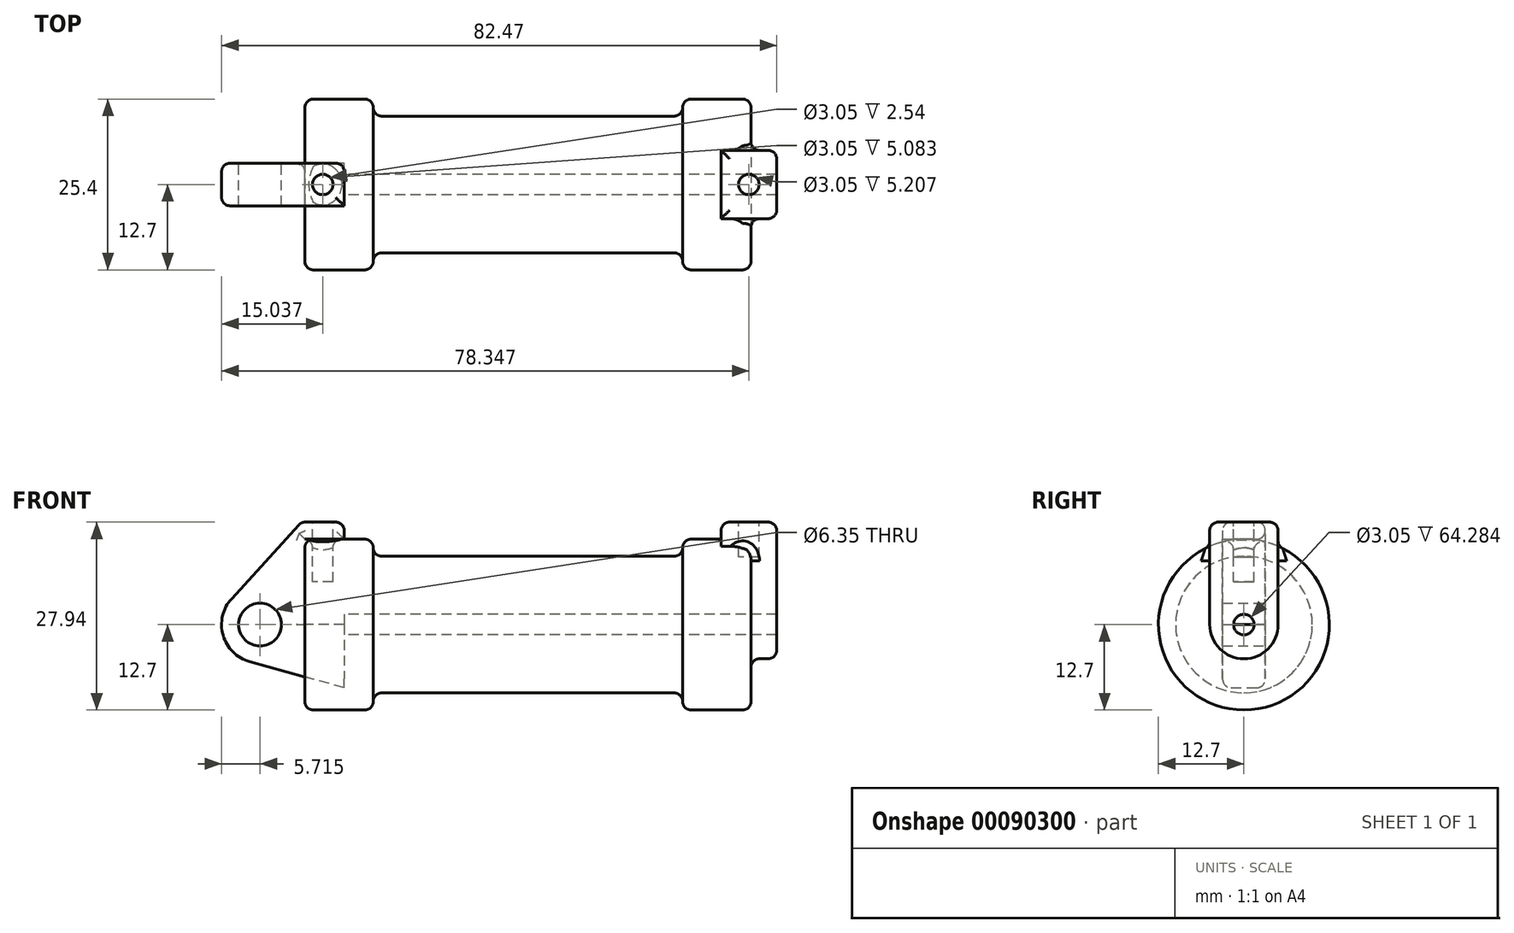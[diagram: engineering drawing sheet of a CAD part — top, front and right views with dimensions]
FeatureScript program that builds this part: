
annotation { "Feature Type Name" : "Feature", "Feature Type Description" : "" }
export const myFeature = defineFeature(function(context is Context, id is Id, definition is map)
    precondition{}
    {
        {
            var Q0;
            Q0=qCreatedBy(makeId("Front.planeOp"),FACE);
            var sketch = newSketch(context, id + "F0", { "sketchPlane" : qUnion([Q0])});
            skLineSegment(sketch, "E0", {"start": v(0, 0) * mm, "end": v(0, 12.7) * mm});
            skLineSegment(sketch, "E1", {"start": v(0, 12.7) * mm, "end": v(10.16, 12.7) * mm});
            skLineSegment(sketch, "E2", {"start": v(10.16, 12.7) * mm, "end": v(10.16, 10.16) * mm});
            skLineSegment(sketch, "E3", {"start": v(10.16, 10.16) * mm, "end": v(56.13, 10.16) * mm});
            skLineSegment(sketch, "E4", {"start": v(56.13, 10.16) * mm, "end": v(56.13, 12.7) * mm});
            skLineSegment(sketch, "E5", {"start": v(56.13, 12.7) * mm, "end": v(66.3, 12.7) * mm});
            skLineSegment(sketch, "E6", {"start": v(66.3, 12.7) * mm, "end": v(66.3, 0) * mm});
            skLineSegment(sketch, "E7", {"start": v(66.3, 0) * mm, "end": v(0, 0) * mm});
            skLineSegment(sketch, "E8", {"start": v(5.84, 15.24) * mm, "end": v(-0.5, 15.24) * mm});
            skLineSegment(sketch, "E9", {"start": v(-0.5, 15.24) * mm, "end": v(-10.88, 3.85) * mm});
            skLineSegment(sketch, "E10", {"start": v(0, 0) * mm, "end": v(-6.65, 0) * mm});
            skCircle(sketch, "E11", {"center": v(-6.65, 0) * mm, "radius": 5.72 * mm});
            skCircle(sketch, "E12", {"center": v(-6.65, 0) * mm, "radius": 3.18 * mm});
            skLineSegment(sketch, "E13", {"start": v(5.84, 15.24) * mm, "end": v(5.84, -9.4) * mm});
            skLineSegment(sketch, "E14", {"start": v(5.84, -9.4) * mm, "end": v(-8.18, -5.5) * mm});
            skSolve(sketch);
        }
        {
            var Q0;
            {var subQ0=sQuery(id+"F0.wireOp",EDGE,"E2");Q0=makeQuery(id+"F0.imprint","IMPRINT",FACE,{"disambiguationData":[TD([[makeQuery(id+"F0.imprint","IMPRINT",EDGE,{"derivedFrom":subQ0}),-1.0]])]});}
            var Q1;
            {var subQ0=sQuery(id+"F0.wireOp",EDGE,"E0");Q1=makeQuery(id+"F0.imprint","IMPRINT",FACE,{"disambiguationData":[TD([[makeQuery(id+"F0.imprint","IMPRINT",EDGE,{"derivedFrom":subQ0}),-1.0]])]});}
            var Q2;
            Q2=sQuery(id+"F0.wireOp",EDGE,"E7");
            revolve(context, id + "F1", {"entities" : qUnion([Q0, Q1]), "axis" : qUnion([Q2]), "revolveType" : RevolveType.FULL});
        }
        {
            var Q0;
            {var subQ3=sQuery(id+"F0.wireOp",EDGE,"E0");Q0=makeQuery(id+"F0.imprint","IMPRINT",FACE,{"disambiguationData":[TD([[makeQuery(id+"F0.imprint","IMPRINT",EDGE,{"derivedFrom":subQ3}),1.0]])]});}
            var Q1;
            {var subQ0=sQuery(id+"F0.wireOp",EDGE,"E14");Q1=makeQuery(id+"F0.imprint","IMPRINT",FACE,{"disambiguationData":[TD([[makeQuery(id+"F0.imprint","IMPRINT",EDGE,{"derivedFrom":subQ0}),-1.0]])]});}
            var Q2;
            {var subQ4=sQuery(id+"F0.wireOp",EDGE,"E12");Q2=makeQuery(id+"F0.imprint","IMPRINT",FACE,{"disambiguationData":[TD([[makeQuery(id+"F0.imprint","IMPRINT",EDGE,{"derivedFrom":subQ4}),-1.0]])]});}
            extrude(context, id + "F2", {"entities" : qUnion([Q0, Q1, Q2]), "endBound" : BoundingType.SYMMETRIC, "depth" : 6.35 * mm});
        }
        {
            var Q0;
            Q0=makeQuery(id+"F1.opRevolve","SWEPT_FACE",FACE,{"disambiguationData":[OSD([sQuery(id+"F0.wireOp",EDGE,"E6")])]});
            var sketch = newSketch(context, id + "F3", { "sketchPlane" : qUnion([Q0])});
            skCircle(sketch, "E15", {"center": v(0, 0) * mm, "radius": 1.52 * mm});
            skCircle(sketch, "E16", {"center": v(0, 0) * mm, "radius": 5.08 * mm});
            skLineSegment(sketch, "E17", {"start": v(-5.08, 15.24) * mm, "end": v(-5.08, 0) * mm});
            skLineSegment(sketch, "E18", {"start": v(5.08, 15.24) * mm, "end": v(5.08, 0) * mm});
            skLineSegment(sketch, "E19", {"start": v(-5.08, 15.24) * mm, "end": v(5.08, 15.24) * mm});
            skSolve(sketch);
        }
        {
            var Q0;
            {var subQ0=sQuery(id+"F3.wireOp",EDGE,"E19");Q0=makeQuery(id+"F3.imprint","IMPRINT",FACE,{"disambiguationData":[TD([[makeQuery(id+"F3.imprint","IMPRINT",EDGE,{"derivedFrom":subQ0}),-1.0]])]});}
            var Q1;
            {var subQ0=sQuery(id+"F3.wireOp",EDGE,"E17");var subQ1=sQuery(id+"F3.wireOp",EDGE,"E16");var subQ2=makeQuery(id+"F3.imprint","INTERSECT",VERTEX,{"derivedFrom":[subQ1,subQ0]});Q1=makeQuery(id+"F3.imprint","IMPRINT",FACE,{"disambiguationData":[TD([[makeQuery(id+"F3.imprint","IMPRINT",EDGE,{"disambiguationData":[TD([[subQ2,1.0]])],"derivedFrom":subQ1}),-1.0]])]});}
            var Q2;
            Q2=makeQuery(id+"F3.imprint","IMPRINT",FACE,{"disambiguationData":[TD([[makeQuery(id+"F3.imprint","IMPRINT",EDGE,{"derivedFrom":sQuery(id+"F3.wireOp",EDGE,"E15")}),-1.0]])]});
            extrude(context, id + "F4", {"entities" : qUnion([Q0, Q1, Q2]), "operationType" : NewBodyOperationType.ADD, "endBound" : BoundingType.SYMMETRIC, "depth" : 7.62 * mm});
        }
        {
            var Q0;
            Q0=makeQuery(id+"F4.opExtrude","CAP_FACE",FACE,{"disambiguationData":[OSD([sQuery(id+"F3.wireOp",EDGE,"E15"),sQuery(id+"F3.wireOp",EDGE,"E16"),sQuery(id+"F3.wireOp",EDGE,"E17"),sQuery(id+"F3.wireOp",EDGE,"E18"),sQuery(id+"F3.wireOp",EDGE,"E19")])],"isStart":true});
            extrude(context, id + "F5", {"entities" : qUnion([Q0]), "operationType" : NewBodyOperationType.ADD, "endBound" : BoundingType.SYMMETRIC, "depth" : 1.27 * mm});
        }
        {
            var Q0;
            Q0=makeQuery(id+"F4.boolean.opBoolean","SPLIT",FACE,{"disambiguationData":[TD([makeQuery(id+"F4.opExtrude","SWEPT_FACE",FACE,{"disambiguationData":[OSD([sQuery(id+"F3.wireOp",EDGE,"E15")])]})])],"derivedFrom":makeQuery(id+"F1.opRevolve","SWEPT_FACE",FACE,{"disambiguationData":[OSD([sQuery(id+"F0.wireOp",EDGE,"E6")])]})});
            extrude(context, id + "F6", {"entities" : qUnion([Q0]), "operationType" : NewBodyOperationType.REMOVE, "endBound" : BoundingType.SYMMETRIC, "oppositeDirection" : true, "depth" : 120.95 * mm});
        }
        {
            var Q0;
            Q0=makeQuery(id+"F2.opExtrude","SWEPT_FACE",FACE,{"disambiguationData":[OSD([sQuery(id+"F0.wireOp",EDGE,"E8")])]});
            var sketch = newSketch(context, id + "F7", { "sketchPlane" : qUnion([Q0])});
            skCircle(sketch, "E20", {"center": v(2.67, 0) * mm, "radius": 1.52 * mm});
            skPoint(sketch, "E20.centerSnap0", {"position": v(2.67, 3.18) * mm});
            skPoint(sketch, "E20.centerSnap1", {"position": v(-0.5, 0) * mm});
            skSolve(sketch);
        }
        {
            var Q0;
            {var subQ0=sQuery(id+"F3.wireOp",EDGE,"E19");Q0=makeQuery(id+"F5.boolean.opBoolean","MERGE",FACE,{"derivedFrom":[makeQuery(id+"F4.opExtrude","SWEPT_FACE",FACE,{"disambiguationData":[OSD([subQ0])]}),makeQuery(id+"F5.opExtrude","SWEPT_FACE",FACE,{"disambiguationData":[OSD([subQ0])]})]});}
            var sketch = newSketch(context, id + "F8", { "sketchPlane" : qUnion([Q0])});
            skCircle(sketch, "E21", {"center": v(65.98, 0) * mm, "radius": 1.52 * mm});
            skPoint(sketch, "E21.centerSnap0", {"position": v(65.98, 5.08) * mm});
            skPoint(sketch, "E21.centerSnap1", {"position": v(61.85, 0) * mm});
            skSolve(sketch);
        }
        {
            var Q0;
            Q0=makeQuery(id+"F7.imprint","IMPRINT",FACE,{"disambiguationData":[TD([[makeQuery(id+"F7.imprint","IMPRINT",EDGE,{"derivedFrom":sQuery(id+"F7.wireOp",EDGE,"E20")}),1.0]])]});
            extrude(context, id + "F9", {"entities" : qUnion([Q0]), "operationType" : NewBodyOperationType.REMOVE, "endBound" : BoundingType.SYMMETRIC, "oppositeDirection" : true, "depth" : 17.78 * mm});
        }
        {
            var Q0;
            Q0=makeQuery(id+"F8.imprint","IMPRINT",FACE,{"disambiguationData":[TD([[makeQuery(id+"F8.imprint","IMPRINT",EDGE,{"derivedFrom":sQuery(id+"F8.wireOp",EDGE,"E21")}),1.0]])]});
            extrude(context, id + "F10", {"entities" : qUnion([Q0]), "operationType" : NewBodyOperationType.REMOVE, "endBound" : BoundingType.SYMMETRIC, "oppositeDirection" : true, "depth" : 10.4 * mm});
        }
        {
            var Q0;
            Q0=makeQuery(id+"F2.opExtrude","CAP_EDGE",EDGE,{"disambiguationData":[OSD([sQuery(id+"F0.wireOp",EDGE,"E8")])],"isStart":false});
            var Q1;
            Q1=makeQuery(id+"F2.opExtrude","SWEPT_EDGE",EDGE,{"disambiguationData":[OSD([sQuery(id+"F0.wireOp",EDGE,"E8"),sQuery(id+"F0.wireOp",EDGE,"E13")])]});
            var Q2;
            Q2=makeQuery(id+"F2.opExtrude","CAP_EDGE",EDGE,{"disambiguationData":[OSD([sQuery(id+"F0.wireOp",EDGE,"E8")])],"isStart":true});
            var Q3;
            Q3=makeQuery(id+"F2.opExtrude","CAP_EDGE",EDGE,{"disambiguationData":[OSD([sQuery(id+"F0.wireOp",EDGE,"E9")])],"isStart":false});
            var Q4;
            {var subQ0=sQuery(id+"F3.wireOp",EDGE,"E19");var subQ1=sQuery(id+"F3.wireOp",EDGE,"E17");Q4=makeQuery(id+"F5.boolean.opBoolean","MERGE",EDGE,{"derivedFrom":[makeQuery(id+"F4.opExtrude","SWEPT_EDGE",EDGE,{"disambiguationData":[OSD([subQ1,subQ0])]}),makeQuery(id+"F5.opExtrude","SWEPT_EDGE",EDGE,{"disambiguationData":[OSD([subQ1,subQ0])]})]});}
            var Q5;
            Q5=makeQuery(id+"F4.opExtrude","CAP_EDGE",EDGE,{"disambiguationData":[OSD([sQuery(id+"F3.wireOp",EDGE,"E19")])],"isStart":false});
            var Q6;
            {var subQ0=sQuery(id+"F3.wireOp",EDGE,"E19");var subQ1=sQuery(id+"F3.wireOp",EDGE,"E18");Q6=makeQuery(id+"F5.boolean.opBoolean","MERGE",EDGE,{"derivedFrom":[makeQuery(id+"F4.opExtrude","SWEPT_EDGE",EDGE,{"disambiguationData":[OSD([subQ1,subQ0])]}),makeQuery(id+"F5.opExtrude","SWEPT_EDGE",EDGE,{"disambiguationData":[OSD([subQ1,subQ0])]})]});}
            var Q7;
            Q7=makeQuery(id+"F4.opExtrude","CAP_EDGE",EDGE,{"disambiguationData":[OSD([sQuery(id+"F3.wireOp",EDGE,"E17")])],"isStart":false});
            var Q8;
            Q8=makeQuery(id+"F4.opExtrude","CAP_EDGE",EDGE,{"disambiguationData":[OSD([sQuery(id+"F3.wireOp",EDGE,"E18")])],"isStart":false});
            var Q9;
            Q9=makeQuery(id+"F2.opExtrude","SWEPT_EDGE",EDGE,{"disambiguationData":[OSD([sQuery(id+"F0.wireOp",EDGE,"E8"),sQuery(id+"F0.wireOp",EDGE,"E9")])]});
            var Q10;
            Q10=makeQuery(id+"F2.opExtrude","CAP_EDGE",EDGE,{"disambiguationData":[OSD([sQuery(id+"F0.wireOp",EDGE,"E9")])],"isStart":true});
            var Q11;
            Q11=makeQuery(id+"F5.opExtrude","CAP_EDGE",EDGE,{"disambiguationData":[OSD([sQuery(id+"F3.wireOp",EDGE,"E19")])],"isStart":false});
            var Q12;
            {var subQ0=sQuery(id+"F3.wireOp",EDGE,"E18");var subQ1=makeQuery(id+"F4.opExtrude","SWEPT_FACE",FACE,{"disambiguationData":[OSD([subQ0])]});var subQ2=sQuery(id+"F3.wireOp",EDGE,"E19");var subQ3=sQuery(id+"F3.wireOp",EDGE,"E17");var subQ4=sQuery(id+"F3.wireOp",EDGE,"E16");var subQ5=sQuery(id+"F3.wireOp",EDGE,"E15");var subQ6=sQuery(id+"F0.wireOp",EDGE,"E5");var subQ7=makeQuery(id+"F1.opRevolve","SWEPT_FACE",FACE,{"disambiguationData":[OSD([subQ6])]});Q12=makeQuery(id+"F5.boolean.opBoolean","MERGE",EDGE,{"derivedFrom":[makeQuery(id+"F4.boolean.opBoolean","INTERSECT",EDGE,{"derivedFrom":[subQ7,subQ1]}),makeQuery(id+"F5.opExtrude","SWEPT_EDGE",EDGE,{"disambiguationData":[OSD([subQ6,subQ5,subQ4,subQ3,subQ0,subQ2]),TDD([makeQuery(id+"F4.boolean.opBoolean","INTERSECT",VERTEX,{"derivedFrom":[subQ7,makeQuery(id+"F4.opExtrude","CAP_FACE",FACE,{"disambiguationData":[OSD([subQ5,subQ4,subQ3,subQ0,subQ2])],"isStart":true}),subQ1]})])]})]});}
            var Q13;
            Q13=makeQuery(id+"F4.boolean.opBoolean","INTERSECT",EDGE,{"derivedFrom":[makeQuery(id+"F1.opRevolve","SWEPT_FACE",FACE,{"disambiguationData":[OSD([sQuery(id+"F0.wireOp",EDGE,"E6")])]}),makeQuery(id+"F4.opExtrude","SWEPT_FACE",FACE,{"disambiguationData":[OSD([sQuery(id+"F3.wireOp",EDGE,"E18")])]})]});
            var Q14;
            Q14=makeQuery(id+"F4.opExtrude","CAP_EDGE",EDGE,{"disambiguationData":[OSD([sQuery(id+"F3.wireOp",EDGE,"E16")])],"isStart":false});
            var Q15;
            Q15=makeQuery(id+"F1.opRevolve","SWEPT_EDGE",EDGE,{"disambiguationData":[OSD([sQuery(id+"F0.wireOp",EDGE,"E4"),sQuery(id+"F0.wireOp",EDGE,"E5")])]});
            var Q16;
            Q16=makeQuery(id+"F4.boolean.opBoolean","SPLIT",FACE,{"disambiguationData":[TD([makeQuery(id+"F1.opRevolve","SWEPT_FACE",FACE,{"disambiguationData":[OSD([sQuery(id+"F0.wireOp",EDGE,"E5")])]})])],"derivedFrom":makeQuery(id+"F1.opRevolve","SWEPT_FACE",FACE,{"disambiguationData":[OSD([sQuery(id+"F0.wireOp",EDGE,"E6")])]})});
            var Q17;
            Q17=makeQuery(id+"F4.boolean.opBoolean","INTERSECT",EDGE,{"derivedFrom":[makeQuery(id+"F1.opRevolve","SWEPT_FACE",FACE,{"disambiguationData":[OSD([sQuery(id+"F0.wireOp",EDGE,"E6")])]}),makeQuery(id+"F4.opExtrude","SWEPT_FACE",FACE,{"disambiguationData":[OSD([sQuery(id+"F3.wireOp",EDGE,"E16")])]})]});
            var Q18;
            Q18=makeQuery(id+"F2.opExtrude","CAP_EDGE",EDGE,{"disambiguationData":[OSD([sQuery(id+"F0.wireOp",EDGE,"E0")])],"isStart":true});
            var Q19;
            Q19=makeQuery(id+"F2.opExtrude","CAP_EDGE",EDGE,{"disambiguationData":[OSD([sQuery(id+"F0.wireOp",EDGE,"E1")])],"isStart":true});
            var Q20;
            Q20=makeQuery(id+"F2.opExtrude","CAP_EDGE",EDGE,{"disambiguationData":[OSD([sQuery(id+"F0.wireOp",EDGE,"E11")])],"isStart":true});
            var Q21;
            Q21=makeQuery(id+"F2.opExtrude","CAP_EDGE",EDGE,{"disambiguationData":[OSD([sQuery(id+"F0.wireOp",EDGE,"E11")])],"isStart":false});
            var Q22;
            Q22=makeQuery(id+"F2.opExtrude","CAP_EDGE",EDGE,{"disambiguationData":[OSD([sQuery(id+"F0.wireOp",EDGE,"E14")])],"isStart":true});
            var Q23;
            Q23=makeQuery(id+"F1.opRevolve","SWEPT_EDGE",EDGE,{"disambiguationData":[OSD([sQuery(id+"F0.wireOp",EDGE,"E0"),sQuery(id+"F0.wireOp",EDGE,"E1")])]});
            var Q24;
            Q24=makeQuery(id+"F2.opExtrude","CAP_EDGE",EDGE,{"disambiguationData":[OSD([sQuery(id+"F0.wireOp",EDGE,"E14")])],"isStart":false});
            var Q25;
            Q25=makeQuery(id+"F1.opRevolve","SWEPT_FACE",FACE,{"disambiguationData":[OSD([sQuery(id+"F0.wireOp",EDGE,"E1")])]});
            var Q26;
            Q26=makeQuery(id+"F1.opRevolve","SWEPT_FACE",FACE,{"disambiguationData":[OSD([sQuery(id+"F0.wireOp",EDGE,"E3")])]});
            var Q27;
            {var subQ0=sQuery(id+"F0.wireOp",EDGE,"E13");Q27=makeQuery(id+"F2.opExtrude","CAP_EDGE",EDGE,{"disambiguationData":[OSD([subQ0]),TDD([makeQuery(id+"F0.imprint","IMPRINT",EDGE,{"disambiguationData":[TD([[makeQuery(id+"F0.imprint","INTERSECT",VERTEX,{"derivedFrom":[sQuery(id+"F0.wireOp",EDGE,"E8"),subQ0]}),-1.0]])],"derivedFrom":subQ0})])],"isStart":true});}
            fillet(context, id + "F11", {"entities" : qUnion([Q0, Q1, Q2, Q3, Q4, Q5, Q6, Q7, Q8, Q9, Q10, Q11, Q12, Q13, Q14, Q15, Q16, Q17, Q18, Q19, Q20, Q21, Q22, Q23, Q24, Q25, Q26, Q27]), "radius" : 1.27 * mm, "tangentPropagation" : true, "allowEdgeOverflow" : false});
        }
    });
